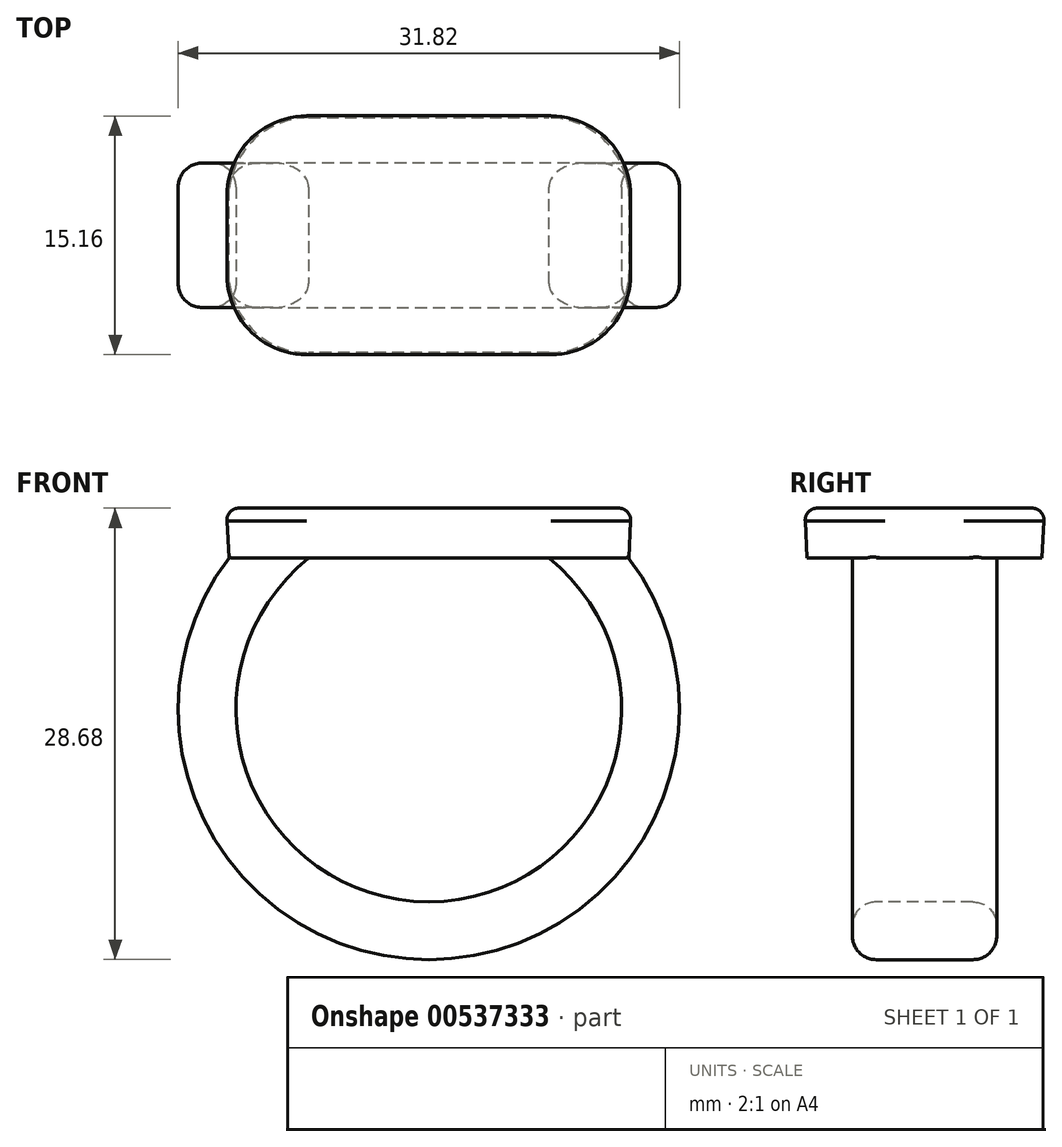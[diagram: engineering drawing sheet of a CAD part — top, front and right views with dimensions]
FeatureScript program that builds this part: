
annotation { "Feature Type Name" : "Feature", "Feature Type Description" : "" }
export const myFeature = defineFeature(function(context is Context, id is Id, definition is map)
    precondition{}
    {
        {
            var Q0;
            Q0=qCreatedBy(makeId("Top.planeOp"),FACE);
            var sketch = newSketch(context, id + "F0", { "sketchPlane" : qUnion([Q0])});
            skLineSegment(sketch, "E0.bottom", {"start": v(-12.7, 7.46) * mm, "end": v(12.7, 7.46) * mm});
            skLineSegment(sketch, "E0.top", {"start": v(-12.7, -7.46) * mm, "end": v(12.7, -7.46) * mm});
            skLineSegment(sketch, "E0.left", {"start": v(-12.7, 7.46) * mm, "end": v(-12.7, -7.46) * mm});
            skLineSegment(sketch, "E0.right", {"start": v(12.7, 7.46) * mm, "end": v(12.7, -7.46) * mm});
            skPoint(sketch, "E0.middle", {"position": v(0, 0) * mm});
            skSolve(sketch);
        }
        {
            var Q0;
            Q0 = qSketchRegion(id + "F0", true);
            extrude(context, id + "F1", {"entities" : qUnion([Q0]), "depth" : 3.17 * mm, "offsetDistance" : 25.4 * mm, "hasDraft" : true, "draftAngle" : 3 * degree});
        }
        {
            var Q0;
            Q0=qCreatedBy(makeId("Front.planeOp"),FACE);
            var sketch = newSketch(context, id + "F2", { "sketchPlane" : qUnion([Q0])});
            skArc(sketch, "E1", {"start": v(-10.16, 0) * mm, "mid": v(0, -23.56) * mm, "end": v(10.16, 0) * mm});
            skSolve(sketch);
        }
        {
            var Q0;
            Q0=makeQuery(id+"F1.opExtrude","CAP_FACE",FACE,{"disambiguationData":[OSD([sQuery(id+"F0.wireOp",EDGE,"E0.bottom"),sQuery(id+"F0.wireOp",EDGE,"E0.top"),sQuery(id+"F0.wireOp",EDGE,"E0.left"),sQuery(id+"F0.wireOp",EDGE,"E0.right")])],"isStart":true});
            var sketch = newSketch(context, id + "F3", { "sketchPlane" : qUnion([Q0])});
            skLineSegment(sketch, "E2.bottom", {"start": v(-7.62, -4.6) * mm, "end": v(-12.7, -4.6) * mm});
            skLineSegment(sketch, "E2.top", {"start": v(-7.62, 4.6) * mm, "end": v(-12.7, 4.6) * mm});
            skLineSegment(sketch, "E2.left", {"start": v(-7.62, -4.6) * mm, "end": v(-7.62, 4.6) * mm});
            skLineSegment(sketch, "E2.right", {"start": v(-12.7, -4.6) * mm, "end": v(-12.7, 4.6) * mm});
            skPoint(sketch, "E2.middle", {"position": v(-10.16, 0) * mm});
            skSolve(sketch);
        }
        {
            var Q0;
            Q0 = qSketchRegion(id + "F3", true);
            var Q1;
            Q1 = qConstructionFilter(qBodyType(qCreatedBy(id + "F2" ,EDGE), BodyType.WIRE), ConstructionObject.NO);
            sweep(context, id + "F4", {"operationType" : NewBodyOperationType.ADD, "profiles" : qUnion([Q0]), "path" : qUnion([Q1])});
        }
        {
            var Q0;
            Q0=qCreatedBy(makeId("Front.planeOp"),FACE);
            var sketch = newSketch(context, id + "F5", { "sketchPlane" : qUnion([Q0])});
            skLineSegment(sketch, "E3.1", {"start": v(10.01, -2.54) * mm, "end": v(10.16, 0) * mm});
            skArc(sketch, "E3.2", {"start": v(10.01, -2.54) * mm, "mid": v(8.9, -1.18) * mm, "end": v(7.62, 0) * mm});
            skLineSegment(sketch, "E4.trimOffspring", {"start": v(7.62, 0) * mm, "end": v(10.16, 0) * mm});
            skPoint(sketch, "E5.orphan", {"position": v(12.7, 0) * mm});
            skPoint(sketch, "E3.0.end.orphan", {"position": v(-7.62, 0) * mm});
            skPoint(sketch, "E3.0.start.orphan", {"position": v(-12.7, 0) * mm});
            skSolve(sketch);
        }
        {
            var Q0;
            Q0 = qSketchRegion(id + "F5", true);
            var Q1;
            Q1=makeQuery(id+"F4.opSweep","SWEPT_FACE",FACE,{"disambiguationData":[OSD([sQuery(id+"F2.wireOp",EDGE,"E1"),sQuery(id+"F3.wireOp",EDGE,"E2.top")])]});
            var Q2;
            Q2=makeQuery(id+"F4.opSweep","SWEPT_FACE",FACE,{"disambiguationData":[OSD([sQuery(id+"F2.wireOp",EDGE,"E1"),sQuery(id+"F3.wireOp",EDGE,"E2.bottom")])]});
            extrude(context, id + "F6", {"entities" : qUnion([Q0]), "operationType" : NewBodyOperationType.ADD, "endBound" : BoundingType.UP_TO_SURFACE, "depth" : 25.4 * mm, "endBoundEntityFace" : qUnion([Q1]), "offsetDistance" : 25.4 * mm, "hasSecondDirection" : true, "secondDirectionBound" : SecondDirectionBoundingType.UP_TO_SURFACE, "secondDirectionOppositeDirection" : true, "secondDirectionDepth" : 25.4 * mm, "secondDirectionBoundEntityFace" : qUnion([Q2])});
        }
        {
            var Q0;
            Q0=makeQuery(id+"F1.opExtrude","SWEPT_EDGE",EDGE,{"disambiguationData":[OSD([sQuery(id+"F0.wireOp",EDGE,"E0.top"),sQuery(id+"F0.wireOp",EDGE,"E0.left")])]});
            var Q1;
            Q1=makeQuery(id+"F1.opExtrude","SWEPT_EDGE",EDGE,{"disambiguationData":[OSD([sQuery(id+"F0.wireOp",EDGE,"E0.bottom"),sQuery(id+"F0.wireOp",EDGE,"E0.left")])]});
            var Q2;
            Q2=makeQuery(id+"F1.opExtrude","SWEPT_EDGE",EDGE,{"disambiguationData":[OSD([sQuery(id+"F0.wireOp",EDGE,"E0.bottom"),sQuery(id+"F0.wireOp",EDGE,"E0.right")])]});
            var Q3;
            Q3=makeQuery(id+"F1.opExtrude","SWEPT_EDGE",EDGE,{"disambiguationData":[OSD([sQuery(id+"F0.wireOp",EDGE,"E0.top"),sQuery(id+"F0.wireOp",EDGE,"E0.right")])]});
            fillet(context, id + "F7", {"entities" : qUnion([Q0, Q1, Q2, Q3]), "radius" : 5.08 * mm, "tangentPropagation" : true, "allowEdgeOverflow" : false});
        }
        {
            var Q0;
            {var subQ0=sQuery(id+"F3.wireOp",EDGE,"E2.top");var subQ1=sQuery(id+"F2.wireOp",EDGE,"E1");Q0=makeQuery(id+"F6.boolean.opBoolean","MERGE",EDGE,{"derivedFrom":[makeQuery(id+"F4.opSweep","SWEPT_EDGE",EDGE,{"disambiguationData":[OSD([subQ1,subQ0,sQuery(id+"F3.wireOp",EDGE,"E2.left")])]}),makeQuery(id+"F6.opExtrude","TWEAK_EDGE",EDGE,{"derivedFrom":[makeQuery(id+"F4.opSweep","SWEPT_FACE",FACE,{"disambiguationData":[OSD([subQ1,subQ0])]}),makeQuery(id+"F5.imprint","IMPRINT",EDGE,{"derivedFrom":sQuery(id+"F5.wireOp",EDGE,"E3.2")})]})]});}
            var Q1;
            Q1=makeQuery(id+"F4.opSweep","SWEPT_EDGE",EDGE,{"disambiguationData":[OSD([sQuery(id+"F0.wireOp",EDGE,"E0.left"),sQuery(id+"F2.wireOp",EDGE,"E1"),sQuery(id+"F3.wireOp",EDGE,"E2.top"),sQuery(id+"F3.wireOp",EDGE,"E2.right")])]});
            var Q2;
            Q2=makeQuery(id+"F4.opSweep","SWEPT_EDGE",EDGE,{"disambiguationData":[OSD([sQuery(id+"F0.wireOp",EDGE,"E0.left"),sQuery(id+"F2.wireOp",EDGE,"E1"),sQuery(id+"F3.wireOp",EDGE,"E2.bottom"),sQuery(id+"F3.wireOp",EDGE,"E2.right")])]});
            var Q3;
            {var subQ0=sQuery(id+"F3.wireOp",EDGE,"E2.bottom");var subQ1=sQuery(id+"F2.wireOp",EDGE,"E1");Q3=makeQuery(id+"F6.boolean.opBoolean","MERGE",EDGE,{"derivedFrom":[makeQuery(id+"F4.opSweep","SWEPT_EDGE",EDGE,{"disambiguationData":[OSD([subQ1,subQ0,sQuery(id+"F3.wireOp",EDGE,"E2.left")])]}),makeQuery(id+"F6.opExtrude","TWEAK_EDGE",EDGE,{"derivedFrom":[makeQuery(id+"F4.opSweep","SWEPT_FACE",FACE,{"disambiguationData":[OSD([subQ1,subQ0])]}),makeQuery(id+"F5.imprint","IMPRINT",EDGE,{"derivedFrom":sQuery(id+"F5.wireOp",EDGE,"E3.2")})]})]});}
            fillet(context, id + "F8", {"entities" : qUnion([Q0, Q1, Q2, Q3]), "radius" : 1.52 * mm, "tangentPropagation" : true, "allowEdgeOverflow" : false});
        }
        {
            var Q0;
            Q0=makeQuery(id+"F1.opExtrude","CAP_FACE",FACE,{"disambiguationData":[OSD([sQuery(id+"F0.wireOp",EDGE,"E0.bottom"),sQuery(id+"F0.wireOp",EDGE,"E0.top"),sQuery(id+"F0.wireOp",EDGE,"E0.left"),sQuery(id+"F0.wireOp",EDGE,"E0.right")])],"isStart":false});
            fillet(context, id + "F9", {"entities" : qUnion([Q0]), "radius" : 0.76 * mm, "tangentPropagation" : true, "allowEdgeOverflow" : false});
        }
    });
